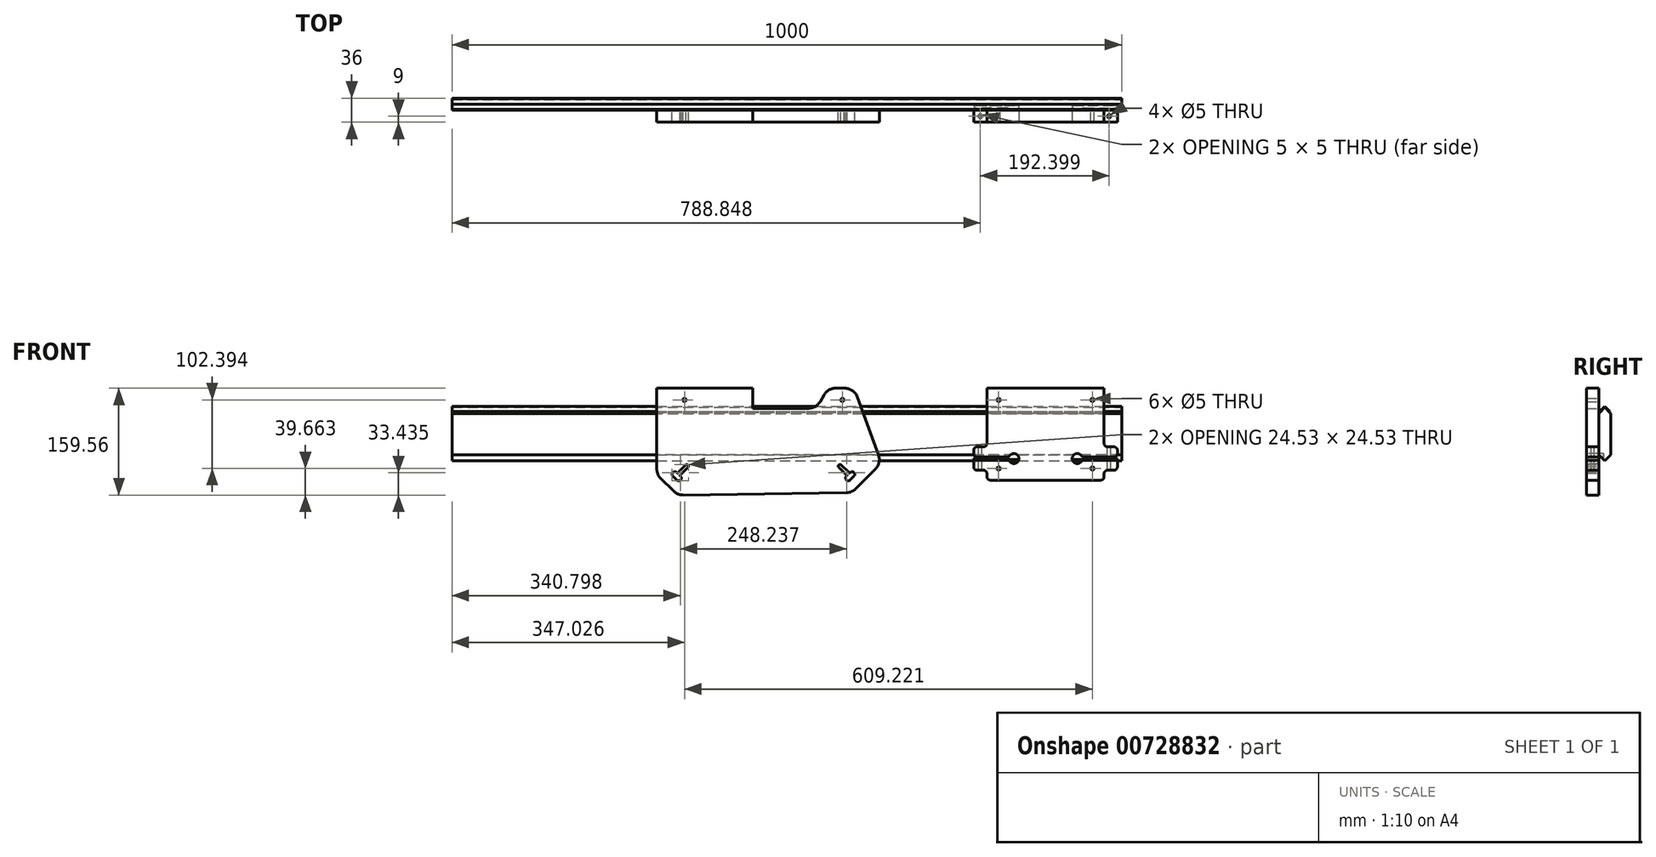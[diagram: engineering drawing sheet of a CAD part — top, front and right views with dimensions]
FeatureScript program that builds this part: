
annotation { "Feature Type Name" : "Feature", "Feature Type Description" : "" }
export const myFeature = defineFeature(function(context is Context, id is Id, definition is map)
    precondition{}
    {
        {
            assignVariable(context, id + "F0", {"name" : "x", "anyValue" : 18});
        }
        {
            var Q0;
            Q0=qCreatedBy(makeId("Right.planeOp"),FACE);
            var sketch = newSketch(context, id + "F1", { "sketchPlane" : qUnion([Q0])});
            skLineSegment(sketch, "E0.bottom", {"start": v(-18, 80) * mm, "end": v(0, 80) * mm});
            skLineSegment(sketch, "E0.top", {"start": v(-18, 0) * mm, "end": v(0, 0) * mm});
            skLineSegment(sketch, "E0.left", {"start": v(-18, 80) * mm, "end": v(-18, 0) * mm});
            skLineSegment(sketch, "E0.right", {"start": v(0, 80) * mm, "end": v(0, 0) * mm});
            skSolve(sketch);
        }
        {
            var Q0;
            Q0 = qSketchRegion(id + "F1", true);
            extrude(context, id + "F2", {"entities" : qUnion([Q0]), "depth" : 1000 * mm, "offsetDistance" : 25 * mm});
        }
        {
            var Q0;
            Q0=makeQuery(id+"F2.opExtrude","SWEPT_EDGE",EDGE,{"disambiguationData":[OSD([sQuery(id+"F1.wireOp",EDGE,"E0.bottom"),sQuery(id+"F1.wireOp",EDGE,"E0.left")])]});
            var Q1;
            Q1=makeQuery(id+"F2.opExtrude","SWEPT_EDGE",EDGE,{"disambiguationData":[OSD([sQuery(id+"F1.wireOp",EDGE,"E0.bottom"),sQuery(id+"F1.wireOp",EDGE,"E0.right")])]});
            var Q2;
            Q2=makeQuery(id+"F2.opExtrude","SWEPT_EDGE",EDGE,{"disambiguationData":[OSD([sQuery(id+"F1.wireOp",EDGE,"E0.top"),sQuery(id+"F1.wireOp",EDGE,"E0.right")])]});
            var Q3;
            Q3=makeQuery(id+"F2.opExtrude","SWEPT_EDGE",EDGE,{"disambiguationData":[OSD([sQuery(id+"F1.wireOp",EDGE,"E0.top"),sQuery(id+"F1.wireOp",EDGE,"E0.left")])]});
            chamfer(context, id + "F3", {"entities" : qUnion([Q0, Q1, Q2, Q3]), "width" : 9 * mm, "tangentPropagation" : true});
        }
        {
            var Q0;
            Q0=makeQuery(id+"F2.opExtrude","CAP_FACE",FACE,{"disambiguationData":[OSD([sQuery(id+"F1.wireOp",EDGE,"E0.bottom"),sQuery(id+"F1.wireOp",EDGE,"E0.top"),sQuery(id+"F1.wireOp",EDGE,"E0.left"),sQuery(id+"F1.wireOp",EDGE,"E0.right")])],"isStart":false});
            var sketch = newSketch(context, id + "F4", { "sketchPlane" : qUnion([Q0])});
            skLineSegment(sketch, "E1", {"start": v(-16.07, 72.93) * mm, "end": v(-16.92, 73.78) * mm});
            skLineSegment(sketch, "E2", {"start": v(-16.92, 73.78) * mm, "end": v(-9, 81.7) * mm});
            skLineSegment(sketch, "E3", {"start": v(-9, 81.7) * mm, "end": v(-1.08, 73.78) * mm});
            skLineSegment(sketch, "E4", {"start": v(-1.08, 73.78) * mm, "end": v(-1.93, 72.93) * mm});
            skLineSegment(sketch, "E5", {"start": v(-1.93, 72.93) * mm, "end": v(-9, 80) * mm});
            skLineSegment(sketch, "E6", {"start": v(-9, 80) * mm, "end": v(-16.07, 72.93) * mm});
            skLineSegment(sketch, "E7", {"start": v(-18, 40) * mm, "end": v(0, 40) * mm, "construction": true});
            skLineSegment(sketch, "E8.MirrorCS", {"start": v(-1.08, 6.22) * mm, "end": v(-1.93, 7.07) * mm, "construction": true});
            skLineSegment(sketch, "E9.MirrorCS", {"start": v(-16.07, 7.07) * mm, "end": v(-16.92, 6.22) * mm, "construction": true});
            skLineSegment(sketch, "E10.MirrorCS", {"start": v(-1.93, 7.07) * mm, "end": v(-9, 0) * mm, "construction": true});
            skLineSegment(sketch, "E11.MirrorCS", {"start": v(-9, 0) * mm, "end": v(-16.07, 7.07) * mm, "construction": true});
            skLineSegment(sketch, "E12.MirrorCS", {"start": v(-16.92, 6.22) * mm, "end": v(-9, -1.7) * mm, "construction": true});
            skLineSegment(sketch, "E13.MirrorCS", {"start": v(-9, -1.7) * mm, "end": v(-1.08, 6.22) * mm, "construction": true});
            skSolve(sketch);
        }
        {
            var Q0;
            Q0 = qSketchRegion(id + "F4", true);
            extrude(context, id + "F5", {"entities" : qUnion([Q0]), "oppositeDirection" : true, "depth" : 1000 * mm, "offsetDistance" : 25 * mm});
        }
        {
            var Q0;
            Q0=makeQuery(id+"F2.opExtrude","SWEPT_FACE",FACE,{"disambiguationData":[OSD([sQuery(id+"F1.wireOp",EDGE,"E0.left")])]});
            var sketch = newSketch(context, id + "F6", { "sketchPlane" : qUnion([Q0])});
            skLineSegment(sketch, "E14.bottom", {"start": v(798.75, 108.7) * mm, "end": v(973.75, 108.7) * mm});
            skLineSegment(sketch, "E14.top", {"start": v(798.75, -28.7) * mm, "end": v(973.75, -28.7) * mm});
            skLineSegment(sketch, "E14.left", {"start": v(798.75, 108.7) * mm, "end": v(798.75, -28.7) * mm});
            skLineSegment(sketch, "E14.right", {"start": v(973.75, 108.7) * mm, "end": v(973.75, -28.7) * mm});
            skLineSegment(sketch, "E15", {"start": v(1000, 40) * mm, "end": v(973.75, 40) * mm, "construction": true});
            skCircle(sketch, "E16", {"center": v(956.25, 91.2) * mm, "radius": 2.5 * mm});
            skCircle(sketch, "E17", {"center": v(956.25, -11.2) * mm, "radius": 2.5 * mm});
            skLineSegment(sketch, "E18", {"start": v(956.25, -11.2) * mm, "end": v(956.25, 91.2) * mm, "construction": true});
            skLineSegment(sketch, "E19", {"start": v(973.75, 40) * mm, "end": v(956.25, 40) * mm, "construction": true});
            skLineSegment(sketch, "E20", {"start": v(886.25, 108.7) * mm, "end": v(886.25, -28.7) * mm, "construction": true});
            skCircle(sketch, "E21.MirrorC", {"center": v(816.25, 91.2) * mm, "radius": 2.5 * mm});
            skCircle(sketch, "E22.MirrorC", {"center": v(816.25, -11.2) * mm, "radius": 2.5 * mm});
            skLineSegment(sketch, "E23.top", {"start": v(798.75, 21.08) * mm, "end": v(778.95, 21.08) * mm});
            skLineSegment(sketch, "E23.left", {"start": v(798.75, -28.7) * mm, "end": v(798.75, 21.08) * mm});
            skLineSegment(sketch, "E23.right", {"start": v(778.95, -13.92) * mm, "end": v(778.95, 21.08) * mm});
            skLineSegment(sketch, "E24.MirrorCS", {"start": v(993.55, -13.92) * mm, "end": v(993.55, 21.08) * mm});
            skLineSegment(sketch, "E25.MirrorCS", {"start": v(973.75, 21.08) * mm, "end": v(993.55, 21.08) * mm});
            skLineSegment(sketch, "E26.MirrorCS", {"start": v(973.75, -28.7) * mm, "end": v(973.75, 21.08) * mm});
            skLineSegment(sketch, "E27", {"start": v(778.95, -13.92) * mm, "end": v(798.75, -13.92) * mm});
            skLineSegment(sketch, "E28.MirrorCS", {"start": v(993.55, -13.92) * mm, "end": v(973.75, -13.92) * mm});
            skSolve(sketch);
        }
        {
            var Q0;
            Q0 = qSketchRegion(id + "F6", true);
            extrude(context, id + "F7", {"entities" : qUnion([Q0]), "depth" : (getVariable(context, 'x')) * mm, "offsetDistance" : 25 * mm});
        }
        {
            var Q0;
            Q0=makeQuery(id+"F7.opExtrude","CAP_FACE",FACE,{"disambiguationData":[OSD([sQuery(id+"F6.wireOp",EDGE,"E14.bottom"),sQuery(id+"F6.wireOp",EDGE,"E14.top"),sQuery(id+"F6.wireOp",EDGE,"E14.left"),sQuery(id+"F6.wireOp",EDGE,"E14.right"),sQuery(id+"F6.wireOp",EDGE,"E16"),sQuery(id+"F6.wireOp",EDGE,"E17"),sQuery(id+"F6.wireOp",EDGE,"E21.MirrorC"),sQuery(id+"F6.wireOp",EDGE,"E22.MirrorC")])],"isStart":false});
            var sketch = newSketch(context, id + "F8", { "sketchPlane" : qUnion([Q0])});
            skLineSegment(sketch, "E29", {"start": v(886.25, -28.7) * mm, "end": v(886.25, 108.7) * mm, "construction": true});
            skLineSegment(sketch, "E30.bottom", {"start": v(778.95, 6.08) * mm, "end": v(838.95, 6.08) * mm});
            skLineSegment(sketch, "E30.top", {"start": v(778.95, 1.08) * mm, "end": v(838.95, 1.08) * mm});
            skLineSegment(sketch, "E30.left", {"start": v(778.95, 6.08) * mm, "end": v(778.95, 1.08) * mm});
            skLineSegment(sketch, "E30.right", {"start": v(838.95, 6.08) * mm, "end": v(838.95, 1.08) * mm});
            skCircle(sketch, "E31", {"center": v(838.95, 3.58) * mm, "radius": 7.5 * mm});
            skLineSegment(sketch, "E32.MirrorCS", {"start": v(933.55, 6.08) * mm, "end": v(933.55, 1.08) * mm});
            skCircle(sketch, "E33.MirrorC", {"center": v(933.55, 3.58) * mm, "radius": 7.5 * mm});
            skLineSegment(sketch, "E34.MirrorCS", {"start": v(993.55, 6.08) * mm, "end": v(933.55, 6.08) * mm});
            skLineSegment(sketch, "E35.MirrorCS", {"start": v(993.55, 1.08) * mm, "end": v(933.55, 1.08) * mm});
            skLineSegment(sketch, "E36.MirrorCS", {"start": v(993.55, 6.08) * mm, "end": v(993.55, 1.08) * mm});
            skLineSegment(sketch, "E37", {"start": v(798.75, -13.92) * mm, "end": v(798.75, 1.08) * mm, "construction": true});
            skPoint(sketch, "E37.endSnap0", {"position": v(808.95, 1.08) * mm});
            skLineSegment(sketch, "E38", {"start": v(798.75, 21.08) * mm, "end": v(798.75, 6.08) * mm, "construction": true});
            skSolve(sketch);
        }
        {
            var Q0;
            Q0 = qSketchRegion(id + "F8", true);
            extrude(context, id + "F9", {"entities" : qUnion([Q0]), "operationType" : NewBodyOperationType.REMOVE, "oppositeDirection" : true, "depth" : 25 * mm, "offsetDistance" : 25 * mm});
        }
        {
            var Q0;
            Q0=makeQuery(id+"F7.opExtrude","SWEPT_EDGE",EDGE,{"disambiguationData":[OSD([sQuery(id+"F6.wireOp",EDGE,"E23.top"),sQuery(id+"F6.wireOp",EDGE,"E23.right")])]});
            var Q1;
            Q1=makeQuery(id+"F7.opExtrude","SWEPT_EDGE",EDGE,{"disambiguationData":[OSD([sQuery(id+"F6.wireOp",EDGE,"E14.left"),sQuery(id+"F6.wireOp",EDGE,"E23.top"),sQuery(id+"F6.wireOp",EDGE,"E23.left")])]});
            var Q2;
            Q2=makeQuery(id+"F9.boolean.opBoolean","COPY",EDGE,{"derivedFrom":makeQuery(id+"F9.opExtrude","SWEPT_EDGE",EDGE,{"disambiguationData":[OSD([sQuery(id+"F6.wireOp",EDGE,"E23.right"),sQuery(id+"F8.wireOp",EDGE,"E30.bottom"),sQuery(id+"F8.wireOp",EDGE,"E30.left")])]})});
            var Q3;
            Q3=makeQuery(id+"F9.boolean.opBoolean","COPY",EDGE,{"derivedFrom":makeQuery(id+"F9.opExtrude","SWEPT_EDGE",EDGE,{"disambiguationData":[OSD([sQuery(id+"F6.wireOp",EDGE,"E23.right"),sQuery(id+"F8.wireOp",EDGE,"E30.top"),sQuery(id+"F8.wireOp",EDGE,"E30.left")])]})});
            var Q4;
            Q4=makeQuery(id+"F9.boolean.opBoolean","COPY",EDGE,{"derivedFrom":makeQuery(id+"F9.opExtrude","SWEPT_EDGE",EDGE,{"disambiguationData":[OSD([sQuery(id+"F8.wireOp",EDGE,"E30.top"),sQuery(id+"F8.wireOp",EDGE,"E31")])]})});
            var Q5;
            Q5=makeQuery(id+"F9.boolean.opBoolean","COPY",EDGE,{"derivedFrom":makeQuery(id+"F9.opExtrude","SWEPT_EDGE",EDGE,{"disambiguationData":[OSD([sQuery(id+"F8.wireOp",EDGE,"E30.bottom"),sQuery(id+"F8.wireOp",EDGE,"E31")])]})});
            var Q6;
            Q6=makeQuery(id+"F7.opExtrude","SWEPT_EDGE",EDGE,{"disambiguationData":[OSD([sQuery(id+"F6.wireOp",EDGE,"E23.bottom"),sQuery(id+"F6.wireOp",EDGE,"E23.right")])]});
            var Q7;
            Q7=makeQuery(id+"F9.boolean.opBoolean","COPY",EDGE,{"derivedFrom":makeQuery(id+"F9.opExtrude","SWEPT_EDGE",EDGE,{"disambiguationData":[OSD([sQuery(id+"F8.wireOp",EDGE,"E33.MirrorC"),sQuery(id+"F8.wireOp",EDGE,"E34.MirrorCS")])]})});
            var Q8;
            Q8=makeQuery(id+"F9.boolean.opBoolean","COPY",EDGE,{"derivedFrom":makeQuery(id+"F9.opExtrude","SWEPT_EDGE",EDGE,{"disambiguationData":[OSD([sQuery(id+"F6.wireOp",EDGE,"E24.MirrorCS"),sQuery(id+"F8.wireOp",EDGE,"E34.MirrorCS"),sQuery(id+"F8.wireOp",EDGE,"E36.MirrorCS")])]})});
            var Q9;
            Q9=makeQuery(id+"F7.opExtrude","SWEPT_EDGE",EDGE,{"disambiguationData":[OSD([sQuery(id+"F6.wireOp",EDGE,"E24.MirrorCS"),sQuery(id+"F6.wireOp",EDGE,"E25.MirrorCS")])]});
            var Q10;
            Q10=makeQuery(id+"F9.boolean.opBoolean","COPY",EDGE,{"derivedFrom":makeQuery(id+"F9.opExtrude","SWEPT_EDGE",EDGE,{"disambiguationData":[OSD([sQuery(id+"F6.wireOp",EDGE,"E24.MirrorCS"),sQuery(id+"F8.wireOp",EDGE,"E35.MirrorCS"),sQuery(id+"F8.wireOp",EDGE,"E36.MirrorCS")])]})});
            var Q11;
            Q11=makeQuery(id+"F7.opExtrude","SWEPT_EDGE",EDGE,{"disambiguationData":[OSD([sQuery(id+"F6.wireOp",EDGE,"9a75249a-1d44-45ec-bdde-61f75abed3f90.MirrorCS"),sQuery(id+"F6.wireOp",EDGE,"E24.MirrorCS")])]});
            var Q12;
            Q12=makeQuery(id+"F7.opExtrude","SWEPT_EDGE",EDGE,{"disambiguationData":[OSD([sQuery(id+"F6.wireOp",EDGE,"E14.right"),sQuery(id+"F6.wireOp",EDGE,"E25.MirrorCS"),sQuery(id+"F6.wireOp",EDGE,"E26.MirrorCS")])]});
            var Q13;
            Q13=makeQuery(id+"F9.boolean.opBoolean","COPY",EDGE,{"derivedFrom":makeQuery(id+"F9.opExtrude","SWEPT_EDGE",EDGE,{"disambiguationData":[OSD([sQuery(id+"F8.wireOp",EDGE,"E33.MirrorC"),sQuery(id+"F8.wireOp",EDGE,"E35.MirrorCS")])]})});
            var Q14;
            Q14=makeQuery(id+"F7.opExtrude","SWEPT_EDGE",EDGE,{"disambiguationData":[OSD([sQuery(id+"F6.wireOp",EDGE,"E23.left"),sQuery(id+"F6.wireOp",EDGE,"E27")])]});
            var Q15;
            Q15=makeQuery(id+"F7.opExtrude","SWEPT_EDGE",EDGE,{"disambiguationData":[OSD([sQuery(id+"F6.wireOp",EDGE,"E14.top"),sQuery(id+"F6.wireOp",EDGE,"E23.left")])]});
            var Q16;
            Q16=makeQuery(id+"F7.opExtrude","SWEPT_EDGE",EDGE,{"disambiguationData":[OSD([sQuery(id+"F6.wireOp",EDGE,"E14.top"),sQuery(id+"F6.wireOp",EDGE,"E26.MirrorCS")])]});
            var Q17;
            Q17=makeQuery(id+"F7.opExtrude","SWEPT_EDGE",EDGE,{"disambiguationData":[OSD([sQuery(id+"F6.wireOp",EDGE,"E26.MirrorCS"),sQuery(id+"F6.wireOp",EDGE,"E28.MirrorCS")])]});
            fillet(context, id + "F10", {"entities" : qUnion([Q0, Q1, Q2, Q3, Q4, Q5, Q6, Q7, Q8, Q9, Q10, Q11, Q12, Q13, Q14, Q15, Q16, Q17]), "radius" : 5 * mm, "tangentPropagation" : true, "allowEdgeOverflow" : false});
        }
        {
            var Q0;
            Q0=makeQuery(id+"F7.opExtrude","SWEPT_FACE",FACE,{"disambiguationData":[OSD([sQuery(id+"F6.wireOp",EDGE,"E23.top")])]});
            var sketch = newSketch(context, id + "F11", { "sketchPlane" : qUnion([Q0])});
            skCircle(sketch, "E39", {"center": v(788.85, -27) * mm, "radius": 2.5 * mm});
            skPoint(sketch, "E39.centerSnap0", {"position": v(788.85, -18) * mm});
            skPoint(sketch, "E39.centerSnap1", {"position": v(783.95, -27) * mm});
            skCircle(sketch, "E40", {"center": v(981.25, -27) * mm, "radius": 2.5 * mm});
            skLineSegment(sketch, "E41", {"start": v(981.25, -27) * mm, "end": v(988.55, -27) * mm, "construction": true});
            skSolve(sketch);
        }
        {
            var Q0;
            Q0 = qSketchRegion(id + "F11", true);
            extrude(context, id + "F12", {"entities" : qUnion([Q0]), "operationType" : NewBodyOperationType.REMOVE, "endBound" : BoundingType.THROUGH_ALL, "oppositeDirection" : true, "depth" : 25 * mm, "offsetDistance" : 25 * mm});
        }
        {
            var Q0;
            Q0=makeQuery(id+"F2.opExtrude","SWEPT_FACE",FACE,{"disambiguationData":[OSD([sQuery(id+"F1.wireOp",EDGE,"E0.left")])]});
            var sketch = newSketch(context, id + "F13", { "sketchPlane" : qUnion([Q0])});
            skLineSegment(sketch, "E42.bottom", {"start": v(305.57, 108.7) * mm, "end": v(448.79, 108.7) * mm});
            skLineSegment(sketch, "E42.left", {"start": v(305.57, 108.7) * mm, "end": v(305.57, -19.93) * mm});
            skLineSegment(sketch, "E42.right", {"start": v(600.38, 108.7) * mm, "end": v(641.08, -3.12) * mm});
            skLineSegment(sketch, "E43", {"start": v(652.7, 71) * mm, "end": v(652.7, 9) * mm, "construction": true});
            skLineSegment(sketch, "E44", {"start": v(652.7, 40) * mm, "end": v(625.38, 40) * mm, "construction": true});
            skCircle(sketch, "E45", {"center": v(582.8, 91.2) * mm, "radius": 2.5 * mm});
            skLineSegment(sketch, "E46", {"start": v(582.8, 91.2) * mm, "end": v(582.8, -11.2) * mm, "construction": true});
            skLineSegment(sketch, "E47", {"start": v(582.8, 40) * mm, "end": v(625.38, 40) * mm, "construction": true});
            skCircle(sketch, "E48", {"center": v(582.8, -11.2) * mm, "radius": 2.5 * mm, "construction": true});
            skLineSegment(sketch, "E49", {"start": v(464.92, -46.9) * mm, "end": v(464.92, 71) * mm, "construction": true});
            skLineSegment(sketch, "E50.top", {"start": v(543.83, 78.7) * mm, "end": v(448.79, 78.7) * mm});
            skLineSegment(sketch, "E50.left", {"start": v(561.16, 108.7) * mm, "end": v(543.83, 78.7) * mm});
            skLineSegment(sketch, "E50.right", {"start": v(448.79, 108.7) * mm, "end": v(448.79, 78.7) * mm});
            skLineSegment(sketch, "E51.trimOffspring", {"start": v(561.16, 108.7) * mm, "end": v(600.38, 108.7) * mm});
            skLineSegment(sketch, "E52", {"start": v(641.08, -3.12) * mm, "end": v(596.95, -47.25) * mm});
            skCircle(sketch, "E53", {"center": v(589.88, -18.27) * mm, "radius": 2.5 * mm});
            skCircle(sketch, "E54", {"center": v(579.27, -7.66) * mm, "radius": 2.5 * mm});
            skLineSegment(sketch, "E55", {"start": v(581.04, -5.9) * mm, "end": v(591.64, -16.5) * mm});
            skLineSegment(sketch, "E56", {"start": v(577.5, -9.43) * mm, "end": v(588.1, -20.04) * mm});
            skLineSegment(sketch, "E57", {"start": v(591.64, -25.69) * mm, "end": v(597.3, -20.03) * mm, "construction": true});
            skLineSegment(sketch, "E58", {"start": v(589.88, -18.27) * mm, "end": v(594.47, -22.86) * mm, "construction": true});
            skArc(sketch, "E59.0.startCap", {"start": v(594.47, -28.52) * mm, "mid": v(588.81, -28.52) * mm, "end": v(588.81, -22.86) * mm});
            skArc(sketch, "E59.0.endCap", {"start": v(594.47, -17.2) * mm, "mid": v(600.13, -17.2) * mm, "end": v(600.13, -22.86) * mm});
            skLineSegment(sketch, "E59.0.left", {"start": v(588.81, -22.86) * mm, "end": v(594.47, -17.2) * mm});
            skLineSegment(sketch, "E59.0.right", {"start": v(594.47, -28.52) * mm, "end": v(600.13, -22.86) * mm});
            skLineSegment(sketch, "E60", {"start": v(336.61, -50.98) * mm, "end": v(596.95, -47.25) * mm});
            skCircle(sketch, "E61.MirrorC", {"center": v(347.03, 91.2) * mm, "radius": 2.5 * mm});
            skLineSegment(sketch, "E62.MirrorCS", {"start": v(341.02, -22.86) * mm, "end": v(335.36, -17.2) * mm});
            skLineSegment(sketch, "E63.MirrorCS", {"start": v(352.33, -9.43) * mm, "end": v(341.72, -20.04) * mm});
            skCircle(sketch, "E64.MirrorC", {"center": v(350.56, -7.66) * mm, "radius": 2.5 * mm});
            skArc(sketch, "E65.MirrorCS", {"start": v(335.36, -28.52) * mm, "mid": v(341.02, -28.52) * mm, "end": v(341.02, -22.86) * mm});
            skLineSegment(sketch, "E66.MirrorCS", {"start": v(348.8, -5.9) * mm, "end": v(338.19, -16.5) * mm});
            skArc(sketch, "E67.MirrorCS", {"start": v(335.36, -17.2) * mm, "mid": v(329.7, -17.2) * mm, "end": v(329.7, -22.86) * mm});
            skLineSegment(sketch, "E68.MirrorCS", {"start": v(335.36, -28.52) * mm, "end": v(329.7, -22.86) * mm});
            skCircle(sketch, "E69.MirrorC", {"center": v(339.95, -18.27) * mm, "radius": 2.5 * mm});
            skLineSegment(sketch, "E70", {"start": v(305.57, -19.93) * mm, "end": v(336.61, -50.98) * mm});
            skSolve(sketch);
        }
        {
            var Q0;
            Q0 = qSketchRegion(id + "F13", true);
            extrude(context, id + "F14", {"entities" : qUnion([Q0]), "depth" : (getVariable(context, 'x')) * mm, "offsetDistance" : 25 * mm});
        }
        {
            var Q0;
            Q0=makeQuery(id+"F14.opExtrude","SWEPT_EDGE",EDGE,{"disambiguationData":[OSD([sQuery(id+"F13.wireOp",EDGE,"E50.left"),sQuery(id+"F13.wireOp",EDGE,"E51.trimOffspring")])]});
            var Q1;
            Q1=makeQuery(id+"F14.opExtrude","SWEPT_EDGE",EDGE,{"disambiguationData":[OSD([sQuery(id+"F13.wireOp",EDGE,"E42.right"),sQuery(id+"F13.wireOp",EDGE,"E51.trimOffspring")])]});
            var Q2;
            Q2=makeQuery(id+"F14.opExtrude","SWEPT_EDGE",EDGE,{"disambiguationData":[OSD([sQuery(id+"F13.wireOp",EDGE,"E50.top"),sQuery(id+"F13.wireOp",EDGE,"E50.left")])]});
            var Q3;
            Q3=makeQuery(id+"F14.opExtrude","SWEPT_EDGE",EDGE,{"disambiguationData":[OSD([sQuery(id+"F13.wireOp",EDGE,"E52"),sQuery(id+"F13.wireOp",EDGE,"E60")])]});
            var Q4;
            Q4=makeQuery(id+"F14.opExtrude","SWEPT_EDGE",EDGE,{"disambiguationData":[OSD([sQuery(id+"F13.wireOp",EDGE,"E60"),sQuery(id+"F13.wireOp",EDGE,"E70")])]});
            var Q5;
            Q5=makeQuery(id+"F14.opExtrude","SWEPT_EDGE",EDGE,{"disambiguationData":[OSD([sQuery(id+"F13.wireOp",EDGE,"E42.left"),sQuery(id+"F13.wireOp",EDGE,"E70")])]});
            var Q6;
            Q6=makeQuery(id+"F14.opExtrude","SWEPT_EDGE",EDGE,{"disambiguationData":[OSD([sQuery(id+"F13.wireOp",EDGE,"E42.right"),sQuery(id+"F13.wireOp",EDGE,"E52")])]});
            fillet(context, id + "F15", {"entities" : qUnion([Q0, Q1, Q2, Q3, Q4, Q5, Q6]), "radius" : 20 * mm, "tangentPropagation" : true, "allowEdgeOverflow" : false});
        }
        {
            var Q0;
            {var subQ0=sQuery(id+"F13.wireOp",EDGE,"E69.MirrorC");var subQ1=sQuery(id+"F13.wireOp",EDGE,"E62.MirrorCS");Q0=makeQuery(id+"F14.opExtrude","SWEPT_EDGE",EDGE,{"disambiguationData":[OSD([subQ1,subQ0]),TDD([makeQuery(id+"F13.imprint","INTERSECT",VERTEX,{"disambiguationData":[OD(0.0)],"derivedFrom":[subQ1,subQ0]})])]});}
            var Q1;
            {var subQ0=sQuery(id+"F13.wireOp",EDGE,"E69.MirrorC");var subQ1=sQuery(id+"F13.wireOp",EDGE,"E62.MirrorCS");Q1=makeQuery(id+"F14.opExtrude","SWEPT_EDGE",EDGE,{"disambiguationData":[OSD([subQ1,subQ0]),TDD([makeQuery(id+"F13.imprint","INTERSECT",VERTEX,{"disambiguationData":[OD(1.0)],"derivedFrom":[subQ1,subQ0]})])]});}
            var Q2;
            {var subQ0=sQuery(id+"F13.wireOp",EDGE,"E59.0.left");var subQ1=sQuery(id+"F13.wireOp",EDGE,"E53");Q2=makeQuery(id+"F14.opExtrude","SWEPT_EDGE",EDGE,{"disambiguationData":[OSD([subQ1,subQ0]),TDD([makeQuery(id+"F13.imprint","INTERSECT",VERTEX,{"disambiguationData":[OD(1.0)],"derivedFrom":[subQ1,subQ0]})])]});}
            var Q3;
            {var subQ0=sQuery(id+"F13.wireOp",EDGE,"E59.0.left");var subQ1=sQuery(id+"F13.wireOp",EDGE,"E53");Q3=makeQuery(id+"F14.opExtrude","SWEPT_EDGE",EDGE,{"disambiguationData":[OSD([subQ1,subQ0]),TDD([makeQuery(id+"F13.imprint","INTERSECT",VERTEX,{"disambiguationData":[OD(0.0)],"derivedFrom":[subQ1,subQ0]})])]});}
            fillet(context, id + "F16", {"entities" : qUnion([Q0, Q1, Q2, Q3]), "radius" : 1 * mm, "tangentPropagation" : true, "allowEdgeOverflow" : false});
        }
    });
